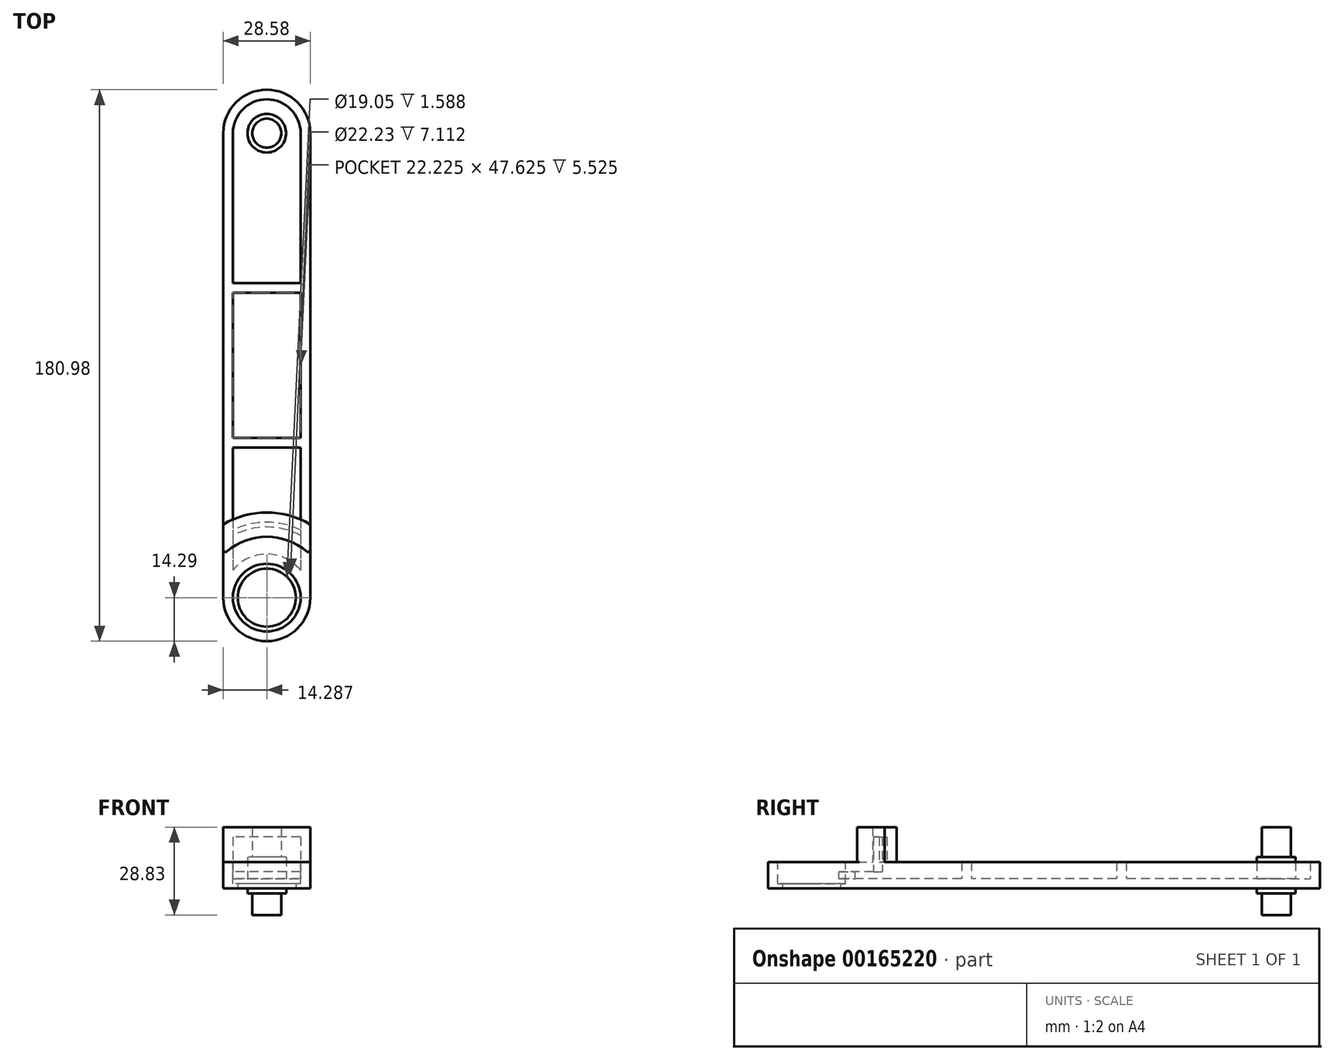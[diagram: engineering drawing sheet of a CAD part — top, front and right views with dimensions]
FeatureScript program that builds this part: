
annotation { "Feature Type Name" : "Feature", "Feature Type Description" : "" }
export const myFeature = defineFeature(function(context is Context, id is Id, definition is map)
    precondition{}
    {
        {
            var Q0;
            Q0=qCreatedBy(makeId("Top.planeOp"),FACE);
            var sketch = newSketch(context, id + "F0", { "sketchPlane" : qUnion([Q0])});
            skLineSegment(sketch, "E0.bottom", {"start": v(0, 0) * mm, "end": v(28.58, 0) * mm, "construction": true});
            skLineSegment(sketch, "E0.top", {"start": v(0, -152.4) * mm, "end": v(28.58, -152.4) * mm, "construction": true});
            skLineSegment(sketch, "E0.left", {"start": v(0, 0) * mm, "end": v(0, -152.4) * mm});
            skLineSegment(sketch, "E0.right", {"start": v(28.58, 0) * mm, "end": v(28.58, -152.4) * mm});
            skArc(sketch, "E1", {"start": v(0, -152.4) * mm, "mid": v(14.29, -166.69) * mm, "end": v(28.58, -152.4) * mm});
            skCircle(sketch, "E2", {"center": v(14.29, -152.4) * mm, "radius": 9.53 * mm});
            skArc(sketch, "E3", {"start": v(28.58, 0) * mm, "mid": v(14.29, 14.29) * mm, "end": v(0, 0) * mm});
            skSolve(sketch);
        }
        {
            var Q0;
            Q0=qSketchRegion(id+"F0",true);
            extrude(context, id + "F1", {"entities" : qUnion([Q0]), "depth" : 8.7 * mm});
        }
        {
            var Q0;
            Q0=makeQuery(id+"F1.opExtrude","CAP_FACE",FACE,{"disambiguationData":[OSD([sQuery(id+"F0.wireOp",EDGE,"E0.left"),sQuery(id+"F0.wireOp",EDGE,"E0.right"),sQuery(id+"F0.wireOp",EDGE,"E1"),sQuery(id+"F0.wireOp",EDGE,"bbfeQyJU-4Eoz-mEa2-qj02-75LyADXawIuP"),sQuery(id+"F0.wireOp",EDGE,"E2")])],"isStart":false});
            var sketch = newSketch(context, id + "F2", { "sketchPlane" : qUnion([Q0])});
            skCircle(sketch, "E4", {"center": v(14.29, -152.4) * mm, "radius": 11.11 * mm});
            skSolve(sketch);
        }
        {
            var Q0;
            Q0=qSketchRegion(id+"F2",true);
            extrude(context, id + "F3", {"entities" : qUnion([Q0]), "operationType" : NewBodyOperationType.REMOVE, "oppositeDirection" : true, "depth" : 7.11 * mm});
        }
        {
            var Q0;
            Q0=makeQuery(id+"F1.opExtrude","CAP_FACE",FACE,{"disambiguationData":[OSD([sQuery(id+"F0.wireOp",EDGE,"E0.left"),sQuery(id+"F0.wireOp",EDGE,"E0.right"),sQuery(id+"F0.wireOp",EDGE,"E1"),sQuery(id+"F0.wireOp",EDGE,"bbfeQyJU-4Eoz-mEa2-qj02-75LyADXawIuP"),sQuery(id+"F0.wireOp",EDGE,"E2")])],"isStart":false});
            var sketch = newSketch(context, id + "F4", { "sketchPlane" : qUnion([Q0])});
            skArc(sketch, "E5", {"start": v(28.57, -138.4) * mm, "mid": v(14.29, -132.39) * mm, "end": v(0, -138.4) * mm});
            skArc(sketch, "E6", {"start": v(28.58, -128.38) * mm, "mid": v(14.29, -124.45) * mm, "end": v(0, -128.38) * mm});
            skLineSegment(sketch, "E7", {"start": v(0, -128.38) * mm, "end": v(0, -138.4) * mm});
            skLineSegment(sketch, "E8", {"start": v(28.58, -128.38) * mm, "end": v(28.58, -138.4) * mm});
            skSolve(sketch);
        }
        {
            var Q0;
            Q0=makeQuery(id+"F4.imprint","IMPRINT",FACE,{"disambiguationData":[TD([[makeQuery(id+"F4.imprint","IMPRINT",EDGE,{"derivedFrom":sQuery(id+"F4.wireOp",EDGE,"E5")}),-1.0]])]});
            extrude(context, id + "F5", {"entities" : qUnion([Q0]), "operationType" : NewBodyOperationType.ADD, "depth" : 11.43 * mm});
        }
        {
            var Q0;
            Q0=makeQuery(id+"F5.opExtrude","SWEPT_EDGE",EDGE,{"disambiguationData":[OSD([sQuery(id+"F0.wireOp",EDGE,"E0.left"),sQuery(id+"F4.wireOp",EDGE,"E5"),sQuery(id+"F4.wireOp",EDGE,"E7")])]});
            var Q1;
            Q1=makeQuery(id+"F5.opExtrude","SWEPT_EDGE",EDGE,{"disambiguationData":[OSD([sQuery(id+"F0.wireOp",EDGE,"E0.right"),sQuery(id+"F4.wireOp",EDGE,"E5"),sQuery(id+"F4.wireOp",EDGE,"E8")])]});
            fillet(context, id + "F6", {"entities" : qUnion([Q0, Q1]), "radius" : 0.76 * mm, "tangentPropagation" : true, "allowEdgeOverflow" : false});
        }
        {
            var Q0;
            Q0=makeQuery(id+"F1.opExtrude","CAP_FACE",FACE,{"disambiguationData":[OSD([sQuery(id+"F0.wireOp",EDGE,"E0.left"),sQuery(id+"F0.wireOp",EDGE,"E0.right"),sQuery(id+"F0.wireOp",EDGE,"E1"),sQuery(id+"F0.wireOp",EDGE,"E2"),sQuery(id+"F0.wireOp",EDGE,"TqOIuOwG-SBgp-Xrd8-DAEF-Dg26LSKY1BrD"),sQuery(id+"F0.wireOp",EDGE,"F2v7sMcf-1XRR-xR4G-D85B-YKigIZ3szwHW"),sQuery(id+"F0.wireOp",EDGE,"0xgYGnf2-QQHX-0xbf-zb4c-rfVaQ3fZe4jW")])],"isStart":true});
            var sketch = newSketch(context, id + "F7", { "sketchPlane" : qUnion([Q0])});
            skCircle(sketch, "E9", {"center": v(14.29, 0) * mm, "radius": 6.35 * mm});
            skSolve(sketch);
        }
        {
            var Q0;
            Q0=qSketchRegion(id+"F7",true);
            extrude(context, id + "F8", {"entities" : qUnion([Q0]), "operationType" : NewBodyOperationType.ADD, "depth" : 1.59 * mm});
        }
        {
            var Q0;
            Q0=makeQuery(id+"F8.opExtrude","CAP_FACE",FACE,{"disambiguationData":[OSD([sQuery(id+"F7.wireOp",EDGE,"E9")])],"isStart":false});
            var sketch = newSketch(context, id + "F9", { "sketchPlane" : qUnion([Q0])});
            skCircle(sketch, "E10", {"center": v(14.29, 0) * mm, "radius": 4.76 * mm});
            skSolve(sketch);
        }
        {
            var Q0;
            Q0=qSketchRegion(id+"F9",true);
            extrude(context, id + "F10", {"entities" : qUnion([Q0]), "operationType" : NewBodyOperationType.ADD, "depth" : 7.11 * mm});
        }
        {
            var Q0;
            {var subQ0=sQuery(id+"F0.wireOp",EDGE,"E3");var subQ1=sQuery(id+"F0.wireOp",EDGE,"E0.right");var subQ2=sQuery(id+"F0.wireOp",EDGE,"E0.left");Q0=makeQuery(id+"F5.boolean.opBoolean","SPLIT",FACE,{"disambiguationData":[TD([makeQuery(id+"F1.opExtrude","SWEPT_FACE",FACE,{"disambiguationData":[OSD([subQ0])]})])],"derivedFrom":makeQuery(id+"F1.opExtrude","CAP_FACE",FACE,{"disambiguationData":[OSD([subQ2,subQ1,sQuery(id+"F0.wireOp",EDGE,"E1"),sQuery(id+"F0.wireOp",EDGE,"E2"),subQ0])],"isStart":false})});}
            shell(context, id + "F11", {"entities" : qUnion([Q0]), "thickness" : 3.17 * mm});
        }
        {
            var Q0;
            {var subQ0=sQuery(id+"F9.wireOp",EDGE,"E10");Q0=makeQuery(id+"F11.opShell","OFFSET_FACE",FACE,{"disambiguationData":[OSD([subQ0]),TDD([makeQuery(id+"F10.opExtrude","CAP_FACE",FACE,{"disambiguationData":[OSD([subQ0])],"isStart":false})])]});}
            var sketch = newSketch(context, id + "F12", { "sketchPlane" : qUnion([Q0])});
            skCircle(sketch, "E11", {"center": v(14.29, 0) * mm, "radius": 4.76 * mm});
            skSolve(sketch);
        }
        {
            var Q0;
            Q0=qSketchRegion(id+"F12",true);
            var Q1;
            Q1=makeQuery(id+"F5.opExtrude","CAP_FACE",FACE,{"disambiguationData":[OSD([sQuery(id+"F4.wireOp",EDGE,"E5"),sQuery(id+"F4.wireOp",EDGE,"E6"),sQuery(id+"F4.wireOp",EDGE,"E7"),sQuery(id+"F4.wireOp",EDGE,"E8")])],"isStart":false});
            extrude(context, id + "F13", {"entities" : qUnion([Q0]), "operationType" : NewBodyOperationType.ADD, "endBound" : BoundingType.UP_TO_SURFACE, "endBoundEntityFace" : qUnion([Q1]), "depth" : 25.4 * mm});
        }
        {
            var Q0;
            {var subQ0=sQuery(id+"F0.wireOp",EDGE,"0xgYGnf2-QQHX-0xbf-zb4c-rfVaQ3fZe4jW");var subQ1=sQuery(id+"F0.wireOp",EDGE,"F2v7sMcf-1XRR-xR4G-D85B-YKigIZ3szwHW");var subQ2=sQuery(id+"F0.wireOp",EDGE,"TqOIuOwG-SBgp-Xrd8-DAEF-Dg26LSKY1BrD");var subQ3=sQuery(id+"F0.wireOp",EDGE,"E2");var subQ4=sQuery(id+"F0.wireOp",EDGE,"E1");var subQ5=sQuery(id+"F0.wireOp",EDGE,"E0.right");var subQ6=sQuery(id+"F0.wireOp",EDGE,"E0.left");Q0=makeQuery(id+"F11.opShell","OFFSET_FACE",FACE,{"disambiguationData":[OSD([subQ6,subQ5,subQ4,subQ3,subQ2,subQ1,subQ0]),TDD([makeQuery(id+"F1.opExtrude","CAP_FACE",FACE,{"disambiguationData":[OSD([subQ6,subQ5,subQ4,subQ3,subQ2,subQ1,subQ0])],"isStart":true})])]});}
            var sketch = newSketch(context, id + "F14", { "sketchPlane" : qUnion([Q0])});
            skCircle(sketch, "E12", {"center": v(14.29, 0) * mm, "radius": 6.35 * mm});
            skSolve(sketch);
        }
        {
            var Q0;
            Q0=qSketchRegion(id+"F14",true);
            extrude(context, id + "F15", {"entities" : qUnion([Q0]), "operationType" : NewBodyOperationType.ADD, "depth" : 7.11 * mm});
        }
        {
            var Q0;
            {var subQ0=sQuery(id+"F0.wireOp",EDGE,"0xgYGnf2-QQHX-0xbf-zb4c-rfVaQ3fZe4jW");var subQ1=sQuery(id+"F0.wireOp",EDGE,"F2v7sMcf-1XRR-xR4G-D85B-YKigIZ3szwHW");var subQ2=sQuery(id+"F0.wireOp",EDGE,"TqOIuOwG-SBgp-Xrd8-DAEF-Dg26LSKY1BrD");var subQ3=sQuery(id+"F0.wireOp",EDGE,"E2");var subQ4=sQuery(id+"F0.wireOp",EDGE,"E1");var subQ5=sQuery(id+"F0.wireOp",EDGE,"E0.right");var subQ6=sQuery(id+"F0.wireOp",EDGE,"E0.left");Q0=makeQuery(id+"F11.opShell","OFFSET_FACE",FACE,{"disambiguationData":[OSD([subQ6,subQ5,subQ4,subQ3,subQ2,subQ1,subQ0]),TDD([makeQuery(id+"F1.opExtrude","CAP_FACE",FACE,{"disambiguationData":[OSD([subQ6,subQ5,subQ4,subQ3,subQ2,subQ1,subQ0])],"isStart":true})])]});}
            var sketch = newSketch(context, id + "F16", { "sketchPlane" : qUnion([Q0])});
            skLineSegment(sketch, "E13", {"start": v(14.29, 0) * mm, "end": v(23.91, -5.56) * mm, "construction": true});
            skLineSegment(sketch, "E14", {"start": v(23.91, -5.56) * mm, "end": v(14.29, 11.11) * mm, "construction": true});
            skLineSegment(sketch, "E15", {"start": v(14.29, 11.11) * mm, "end": v(14.29, 0) * mm, "construction": true});
            skLineSegment(sketch, "E16", {"start": v(14.29, 0) * mm, "end": v(4.66, -5.56) * mm, "construction": true});
            skLineSegment(sketch, "E17", {"start": v(4.66, -5.56) * mm, "end": v(23.91, -5.56) * mm, "construction": true});
            skLineSegment(sketch, "E18", {"start": v(14.29, 11.11) * mm, "end": v(4.66, -5.56) * mm, "construction": true});
            skLineSegment(sketch, "E19.bottom", {"start": v(15.88, 11.11) * mm, "end": v(12.7, 11.11) * mm});
            skLineSegment(sketch, "E19.top", {"start": v(15.87, 0) * mm, "end": v(12.7, 0) * mm});
            skLineSegment(sketch, "E19.left", {"start": v(15.87, 11.11) * mm, "end": v(15.87, 0) * mm});
            skLineSegment(sketch, "E19.right", {"start": v(12.7, 11.11) * mm, "end": v(12.7, 0) * mm});
            skPoint(sketch, "E19.middle", {"position": v(14.29, 5.56) * mm});
            skLineSegment(sketch, "E20.bottom", {"start": v(15.78, 2.7) * mm, "end": v(17.36, -0.06) * mm});
            skLineSegment(sketch, "E20.top", {"start": v(1.59, -5.5) * mm, "end": v(3.17, -8.25) * mm});
            skLineSegment(sketch, "E20.left", {"start": v(15.78, 2.7) * mm, "end": v(1.59, -5.5) * mm});
            skLineSegment(sketch, "E20.right", {"start": v(17.36, -0.06) * mm, "end": v(3.17, -8.25) * mm});
            skPoint(sketch, "E20.middle", {"position": v(9.48, -2.78) * mm});
            skLineSegment(sketch, "E21.bottom", {"start": v(26.99, -5.5) * mm, "end": v(25.4, -8.25) * mm});
            skLineSegment(sketch, "E21.top", {"start": v(12.8, 2.7) * mm, "end": v(11.21, -0.06) * mm});
            skLineSegment(sketch, "E21.left", {"start": v(26.99, -5.5) * mm, "end": v(12.8, 2.7) * mm});
            skLineSegment(sketch, "E21.right", {"start": v(25.4, -8.25) * mm, "end": v(11.21, -0.06) * mm});
            skPoint(sketch, "E21.middle", {"position": v(19.1, -2.78) * mm});
            skLineSegment(sketch, "E22", {"start": v(14.29, 0) * mm, "end": v(14.29, -50.8) * mm, "construction": true});
            skLineSegment(sketch, "E23", {"start": v(14.29, -50.8) * mm, "end": v(14.29, -101.6) * mm, "construction": true});
            skLineSegment(sketch, "E24", {"start": v(14.29, -101.6) * mm, "end": v(14.29, -152.4) * mm, "construction": true});
            skLineSegment(sketch, "E25.bottom", {"start": v(3.18, -52.39) * mm, "end": v(25.4, -52.39) * mm});
            skLineSegment(sketch, "E25.top", {"start": v(3.18, -49.21) * mm, "end": v(25.4, -49.21) * mm});
            skLineSegment(sketch, "E25.left", {"start": v(3.18, -52.39) * mm, "end": v(3.18, -49.21) * mm});
            skLineSegment(sketch, "E25.right", {"start": v(25.4, -52.39) * mm, "end": v(25.4, -49.21) * mm});
            skPoint(sketch, "E25.middle", {"position": v(14.29, -50.8) * mm});
            skLineSegment(sketch, "E26.bottom", {"start": v(3.18, -100.01) * mm, "end": v(25.4, -100.01) * mm});
            skLineSegment(sketch, "E26.top", {"start": v(3.18, -103.19) * mm, "end": v(25.4, -103.19) * mm});
            skLineSegment(sketch, "E26.left", {"start": v(3.18, -100.01) * mm, "end": v(3.18, -103.19) * mm});
            skLineSegment(sketch, "E26.right", {"start": v(25.4, -100.01) * mm, "end": v(25.4, -103.19) * mm});
            skPoint(sketch, "E26.middle", {"position": v(14.29, -101.6) * mm});
            skSolve(sketch);
        }
        {
            var Q0;
            Q0=makeQuery(id+"F16.imprint","IMPRINT",FACE,{"disambiguationData":[TD([[makeQuery(id+"F16.imprint","IMPRINT",EDGE,{"derivedFrom":sQuery(id+"F16.wireOp",EDGE,"E25.bottom")}),1.0]])]});
            var Q1;
            Q1=makeQuery(id+"F16.imprint","IMPRINT",FACE,{"disambiguationData":[TD([[makeQuery(id+"F16.imprint","IMPRINT",EDGE,{"derivedFrom":sQuery(id+"F16.wireOp",EDGE,"E26.bottom")}),-1.0]])]});
            var Q2;
            {var subQ5=sQuery(id+"F16.wireOp",EDGE,"E19.left");var subQ7=makeQuery(id+"F15.opExtrude","CAP_EDGE",EDGE,{"disambiguationData":[OSD([sQuery(id+"F14.wireOp",EDGE,"E12")])],"isStart":true});var subQ8=makeQuery(id+"F16.imprint","INTERSECT",VERTEX,{"derivedFrom":[subQ7,subQ5]});Q2=makeQuery(id+"F16.imprint","IMPRINT",FACE,{"disambiguationData":[TD([[makeQuery(id+"F16.imprint","IMPRINT",EDGE,{"disambiguationData":[TD([[subQ8,-1.0]])],"derivedFrom":subQ7}),-1.0]])]});}
            var Q3;
            {var subQ0=sQuery(id+"F16.wireOp",EDGE,"E20.left");var subQ4=makeQuery(id+"F15.opExtrude","CAP_EDGE",EDGE,{"disambiguationData":[OSD([sQuery(id+"F14.wireOp",EDGE,"E12")])],"isStart":true});var subQ5=makeQuery(id+"F16.imprint","INTERSECT",VERTEX,{"derivedFrom":[subQ4,subQ0]});Q3=makeQuery(id+"F16.imprint","IMPRINT",FACE,{"disambiguationData":[TD([[makeQuery(id+"F16.imprint","IMPRINT",EDGE,{"disambiguationData":[TD([[subQ5,-1.0]])],"derivedFrom":subQ4}),-1.0]])]});}
            var Q4;
            {var subQ0=sQuery(id+"F16.wireOp",EDGE,"E21.left");var subQ4=makeQuery(id+"F15.opExtrude","CAP_EDGE",EDGE,{"disambiguationData":[OSD([sQuery(id+"F14.wireOp",EDGE,"E12")])],"isStart":true});var subQ5=makeQuery(id+"F16.imprint","INTERSECT",VERTEX,{"derivedFrom":[subQ4,subQ0]});Q4=makeQuery(id+"F16.imprint","IMPRINT",FACE,{"disambiguationData":[TD([[makeQuery(id+"F16.imprint","IMPRINT",EDGE,{"disambiguationData":[TD([[subQ5,1.0]])],"derivedFrom":subQ4}),-1.0]])]});}
            var Q5;
            {var subQ0=sQuery(id+"F0.wireOp",EDGE,"E3");var subQ1=sQuery(id+"F0.wireOp",EDGE,"E0.right");var subQ2=sQuery(id+"F0.wireOp",EDGE,"E0.left");Q5=makeQuery(id+"F5.boolean.opBoolean","SPLIT",FACE,{"disambiguationData":[TD([makeQuery(id+"F1.opExtrude","SWEPT_FACE",FACE,{"disambiguationData":[OSD([subQ0])]})])],"derivedFrom":makeQuery(id+"F1.opExtrude","CAP_FACE",FACE,{"disambiguationData":[OSD([subQ2,subQ1,sQuery(id+"F0.wireOp",EDGE,"E1"),sQuery(id+"F0.wireOp",EDGE,"E2"),subQ0])],"isStart":false})});}
            extrude(context, id + "F17", {"entities" : qUnion([Q0, Q1, Q2, Q3, Q4]), "operationType" : NewBodyOperationType.ADD, "endBound" : BoundingType.UP_TO_SURFACE, "endBoundEntityFace" : qUnion([Q5]), "depth" : 25.4 * mm});
        }
    });
